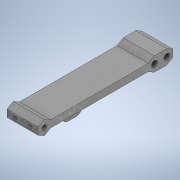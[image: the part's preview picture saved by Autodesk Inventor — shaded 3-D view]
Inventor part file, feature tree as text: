
AUTODESK INVENTOR PART (.ipt)
format: ipt  version: 2020 (Build 240168000, 168)  size: 431,616 bytes
history: native  units: in
note: dims shown in document units (in); Inventor stores cm internally (conversion verified against a paired STEP export)
features: extrude x5, sketch x5, plane x3, projected_geometry x3, mirror x1, fillet x1
ambient origin geometry x8: Origin, YZ Plane, XZ Plane, XY Plane, X Axis, Y Axis, Z Axis, Center Point
bodies: Solid1 (feature_tree)
feature tree (18):
  extrude  "Extrusion1"  Depth=3.4256in
  plane  "Work Plane1"
  extrude  "Extrusion4"  Depth=0.7874in
  plane  "Work Plane2"
  extrude  "Extrusion6"  Depth=3.1106in
  mirror  "Mirror2"
  extrude  "Extrusion8"  Depth=0.315in
  fillet  "Fillet1"  Radius=0.1476in
  sketch  "Sketch11"  dims[d34=0.2362in d35=0.0in d38=0.315in d39=0.2756in d40=-0.3092in d60=1.0994in d61=0.1378in d63=1.1811in d64=0.1575in d65=0.0in d66=0.126in d67=0.1575in d69=0.1949in d70=0.0906in d71=0.3937in d72=0.3937in d73=0.0in]
  plane  "Work Plane3"
  extrude  "Extrusion9"  TaperAngle=0.0deg  [1 undecoded]
  sketch  "Sketch1"  dims[d0=0.1818in d1=3.4256in]
  sketch  "Sketch5"  dims[d2=0.122in d3=0.7874in]
  sketch  "Sketch7"  dims[d4=0.0in d28=3.1106in]
  projected_geometry  "Projected Loop7"
  projected_geometry  "Projected Loop8"
  sketch  "Sketch10"  dims[d29=0.315in d31=0.315in d33=0.1476in]
  projected_geometry  "Projected Loop10"
note: 1 required parameter value undecoded (feature->parameter linkage not recoverable at this tier; creation-order binding heuristic only, values carry confidence <= 0.55)
